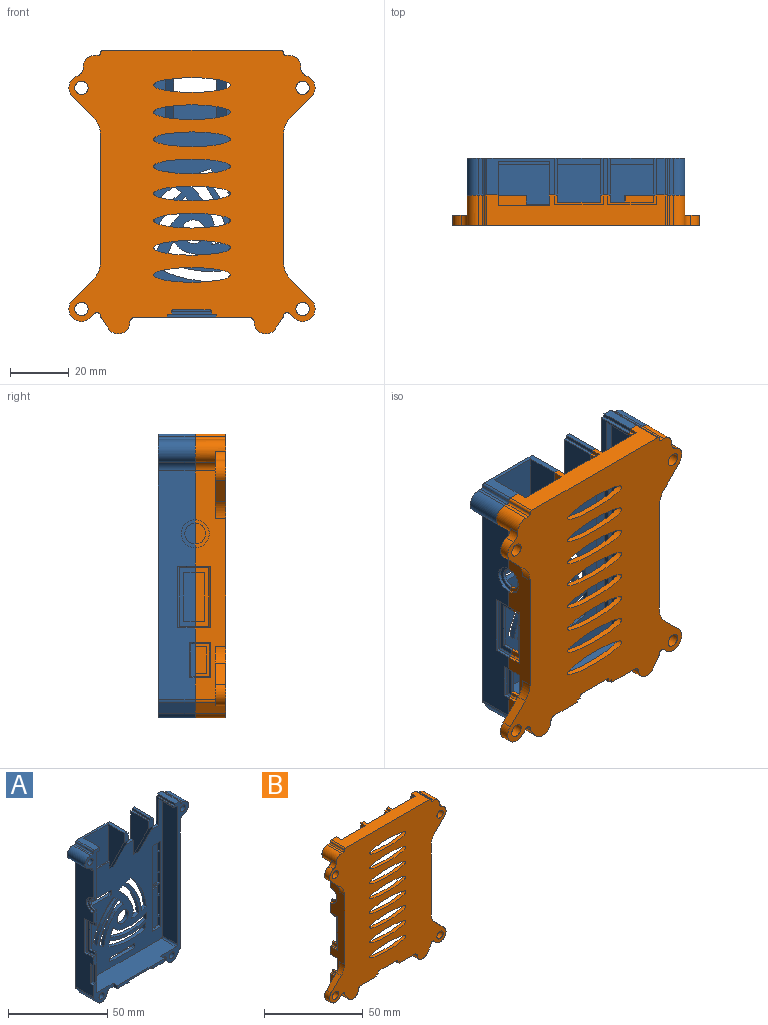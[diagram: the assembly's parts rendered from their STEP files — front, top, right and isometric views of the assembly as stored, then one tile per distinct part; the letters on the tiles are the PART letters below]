
ASSEMBLY  parts=2 mates=1
PART A: 207 faces, bbox 73.8x15.5x96.3 mm
  f0: plane 96.25x73.8mm, normal (0,1,0), area 4343.7mm2, adj f1,f2,f3,f4,f5,f6,f8,f9
  f1: cylinder r=38.11mm len=2.81mm, axis (0,1,0), area 7.6mm2, adj f0,f3,f6,f7
  f2: cylinder r=38.11mm len=3.17mm, axis (0,1,0), area 7.6mm2, adj f0,f7,f27,f28
  f3: cylinder r=34.77mm len=21.39mm, axis (0,-1,0), area 52.8mm2, adj f0,f1,f4,f7
  f4: cylinder r=25.5mm len=2.73mm, axis (0,1,0), area 7mm2, adj f0,f3,f6,f7
  f5: cylinder r=25.5mm len=4.42mm, axis (0,1,0), area 11.1mm2, adj f0,f7,f27,f29
  f6: cylinder r=38.11mm len=21mm, axis (0,1,0), area 52mm2, adj f0,f1,f4,f7
  f7: plane 86.6x58mm, normal (0,-1,0), area 3024.7mm2, adj f1,f2,f3,f4,f5,f6,f8,f9
  f8: cylinder r=38.11mm len=3.71mm, axis (0,1,0), area 7.6mm2, adj f0,f7,f10,f13
  f9: cylinder r=38.11mm len=3.78mm, axis (0,1,0), area 7.6mm2, adj f0,f7,f14,f16
  f10: cylinder r=34.77mm len=25.71mm, axis (0,-1,0), area 52.8mm2, adj f0,f7,f8,f11
  f11: cylinder r=25.5mm len=3.44mm, axis (0,1,0), area 7mm2, adj f0,f7,f10,f13
  f12: cylinder r=25.5mm len=5.08mm, axis (0,1,0), area 11.1mm2, adj f0,f7,f14,f15
  f13: cylinder r=38.11mm len=25.42mm, axis (0,1,0), area 52mm2, adj f0,f7,f8,f11
  f14: cylinder r=32.83mm len=25.5mm, axis (0,-1,0), area 52.5mm2, adj f0,f7,f9,f12
  f15: cylinder r=7.38mm len=4.78mm, axis (0,1,0), area 12.9mm2, adj f0,f7,f12,f16
  f16: cylinder r=29.38mm len=18.77mm, axis (0,1,0), area 38.3mm2, adj f0,f7,f9,f15
  f17: cylinder r=38.11mm len=3.62mm, axis (0,1,0), area 7.6mm2, adj f0,f7,f19,f22
  f18: cylinder r=38.11mm len=3.38mm, axis (0,1,0), area 7.6mm2, adj f0,f7,f23,f25
  f19: cylinder r=34.77mm len=23.14mm, axis (0,-1,0), area 52.8mm2, adj f0,f7,f17,f20
  f20: cylinder r=25.5mm len=3.24mm, axis (0,1,0), area 7mm2, adj f0,f7,f19,f22
  f21: cylinder r=25.5mm len=5.48mm, axis (0,1,0), area 11.1mm2, adj f0,f7,f23,f24
  f22: cylinder r=38.11mm len=23.03mm, axis (0,1,0), area 52mm2, adj f0,f7,f17,f20
  f23: cylinder r=32.83mm len=22.84mm, axis (0,-1,0), area 52.5mm2, adj f0,f7,f18,f21
  f24: cylinder r=7.38mm len=6.15mm, axis (0,1,0), area 12.9mm2, adj f0,f7,f21,f25
  f25: cylinder r=29.38mm len=15.65mm, axis (0,1,0), area 38.3mm2, adj f0,f7,f18,f24
  f26: cylinder r=4mm len=8mm, axis (0,1,0), area 50.3mm2, adj f0,f7
  f27: cylinder r=32.83mm len=21.32mm, axis (0,-1,0), area 52.5mm2, adj f0,f2,f5,f7
  f28: cylinder r=29.38mm len=16.85mm, axis (0,1,0), area 38.3mm2, adj f0,f2,f7,f29
  f29: cylinder r=7.38mm len=5.88mm, axis (0,1,0), area 12.9mm2, adj f0,f5,f7,f28
  f30: plane 16x2mm, normal (0,0,1), area 32mm2, adj f0,f7,f31,f37
  f31: cylinder r=1mm len=2mm, axis (0,-1,0), area 3.1mm2, adj f0,f7,f30,f32
  f32: plane 2x0.8mm, normal (-1,0,0), area 1.6mm2, adj f0,f7,f31,f33
  f33: cylinder r=1mm len=2mm, axis (0,-1,0), area 3.1mm2, adj f0,f7,f32,f34
  f34: plane 16x2mm, normal (0,0,-1), area 32mm2, adj f0,f7,f33,f35
  f35: cylinder r=1mm len=2mm, axis (0,-1,0), area 3.1mm2, adj f0,f7,f34,f36
  f36: plane 2x0.8mm, normal (1,0,0), area 1.6mm2, adj f0,f7,f35,f37
  f37: cylinder r=1mm len=2mm, axis (0,-1,0), area 3.1mm2, adj f0,f7,f30,f36
  f38: plane 2x0.8mm, normal (-1,0,0), area 1.6mm2, adj f0,f7,f39,f45
  f39: cylinder r=1mm len=2mm, axis (0,-1,0), area 3.1mm2, adj f0,f7,f38,f40
  f40: plane 16x2mm, normal (0,0,-1), area 32mm2, adj f0,f7,f39,f41
  f41: cylinder r=1mm len=2mm, axis (0,-1,0), area 3.1mm2, adj f0,f7,f40,f42
  f42: plane 2x0.8mm, normal (1,0,0), area 1.6mm2, adj f0,f7,f41,f43
  f43: cylinder r=1mm len=2mm, axis (0,-1,0), area 3.1mm2, adj f0,f7,f42,f44
  f44: plane 16x2mm, normal (0,0,1), area 32mm2, adj f0,f7,f43,f45
  f45: cylinder r=1mm len=2mm, axis (0,-1,0), area 3.1mm2, adj f0,f7,f38,f44
  f46: cylinder r=1mm len=10.5mm, axis (0,-1,0), area 16.5mm2, adj f7,f47,f50,f55
  f47: plane 10.5x1.55mm, normal (0,0,-1), area 16.3mm2, adj f7,f46,f50,f90
  f48: plane 10.5x1.75mm, normal (0,0,-1), area 18.4mm2, adj f7,f51,f60,f100
  f49: plane 9.75x2.5mm, normal (0,-1,0), area 16.8mm2, adj f55,f104,f110,f111,f112,f113,f114,f115
  f50: plane 30.25x10.45mm, normal (0,-1,0), area 94.5mm2, adj f46,f47,f55,f82,f90,f103,f104,f105
  f51: plane 96.25x20.3mm, normal (0,-1,0), area 270.9mm2, adj f48,f57,f58,f59,f60,f61,f62,f69
  f52: plane 32.75x14.2mm, normal (0,-1,0), area 96.1mm2, adj f55,f56,f57,f62,f68,f104,f115,f116
  f53: plane 6x3.5mm, normal (0,-1,0), area 18.6mm2, adj f80,f83,f85,f93,f94,f95,f96,f98
  f54: plane 6x2.8mm, normal (0,-1,0), area 15.6mm2, adj f82,f84,f86,f87,f88,f102
  f55: plane 84.6x10.5mm, normal (1,0,0), area 682.2mm2, adj f7,f46,f49,f50,f52,f56,f112,f122
  f56: cylinder r=1mm len=10.5mm, axis (0,1,0), area 16.5mm2, adj f7,f52,f55,f57
  f57: plane 56x13.5mm, normal (0,0,1), area 688.2mm2, adj f7,f51,f52,f56,f58,f61,f64,f68
  f58: cylinder r=1mm len=10.5mm, axis (0,1,0), area 16.5mm2, adj f7,f51,f57,f59
  f59: plane 84.6x10.5mm, normal (-1,0,0), area 888.3mm2, adj f7,f51,f58,f60
  f60: cylinder r=1mm len=10.5mm, axis (0,1,0), area 16.5mm2, adj f7,f48,f51,f59
  f61: plane 3x2mm, normal (1,0,0), area 6mm2, adj f51,f57,f62,f64
  f62: plane 38.21x15.5mm, normal (0,0,-1), area 553.1mm2, adj f0,f51,f52,f61,f63,f64,f66,f67
  f63: plane 1.5x1mm, normal (1,0,0), area 1.5mm2, adj f62,f64,f65,f67
  f64: plane 33.4x2mm, normal (0,-1,0), area 50.3mm2, adj f57,f61,f62,f63,f65,f66,f68
  f65: plane 16.5x1.5mm, normal (0,0,-1), area 24.7mm2, adj f63,f64,f66,f67
  f66: plane 1.5x1mm, normal (-1,0,0), area 1.5mm2, adj f62,f64,f65,f67
  f67: plane 16.5x1mm, normal (0,-1,0), area 16.5mm2, adj f62,f63,f65,f66
  f68: plane 3x2mm, normal (-1,0,0), area 6mm2, adj f52,f57,f62,f64
  f69: cylinder r=2mm len=12.5mm, axis (0,1,0), area 38.2mm2, adj f0,f51,f62,f70
  f70: cylinder r=3.9mm len=12.5mm, axis (0,1,0), area 121.2mm2, adj f0,f51,f69,f71
  f71: plane 12.5x3.48mm, normal (0.82,0,-0.58), area 53.1mm2, adj f0,f51,f70,f72
  f72: cylinder r=2mm len=12.5mm, axis (0,1,0), area 15.3mm2, adj f0,f51,f71,f73
  f73: plane 77.46x12.5mm, normal (1,0,0), area 968.2mm2, adj f0,f51,f72,f75
  f74: plane 12.5x0.18mm, normal (1,0,0), area 2.3mm2, adj f0,f51,f78,f79
  f75: cylinder r=3mm len=12.5mm, axis (0,1,0), area 53.5mm2, adj f0,f51,f73,f76
  f76: cylinder r=3.9mm len=12.5mm, axis (0,1,0), area 146.1mm2, adj f0,f51,f75,f77
  f77: plane 12.5x1.2mm, normal (0,0,1), area 15mm2, adj f0,f51,f76,f78
  f78: cylinder r=0.8mm len=12.5mm, axis (0,-1,0), area 15.7mm2, adj f0,f51,f74,f77
  f79: cylinder r=0.8mm len=12.5mm, axis (0,-1,0), area 15.7mm2, adj f0,f51,f74,f81
  f80: plane 12.5x1.5mm, normal (0,0,1), area 18.8mm2, adj f0,f53,f83,f98
  f81: plane 12.5x2.95mm, normal (0,0,1), area 36.9mm2, adj f0,f51,f79,f99
  f82: plane 22.95x12.5mm, normal (0,0,1), area 90.3mm2, adj f0,f50,f54,f88,f90,f91,f102,f103
  f83: plane 12.5x1.2mm, normal (-1,0,0), area 15mm2, adj f0,f53,f80,f85
  f84: plane 12.5x1mm, normal (0,0,1), area 12.5mm2, adj f0,f54,f86,f102
  f85: plane 12.5x1mm, normal (0,0,1), area 12.5mm2, adj f0,f53,f83,f93
  f86: plane 25.8x12.5mm, normal (1,0,0), area 194.7mm2, adj f0,f7,f54,f84,f87,f92
  f87: plane 21x10.5mm, normal (0,-0.89,-0.45), area 65.7mm2, adj f7,f54,f86,f88
  f88: plane 27x11.3mm, normal (-1,0,0), area 191.4mm2, adj f7,f54,f82,f87,f89,f91
  f89: plane 17.4x0.8mm, normal (0,0,1), area 13.9mm2, adj f7,f88,f90,f91
  f90: plane 22.7x11.3mm, normal (1,0,0), area 39.2mm2, adj f7,f47,f50,f82,f89,f91
  f91: plane 22.7x17.4mm, normal (0,-1,0), area 395mm2, adj f82,f88,f89,f90
  f92: plane 14.5x2mm, normal (0,0,1), area 29mm2, adj f0,f7,f86,f93
  f93: plane 25.8x12.5mm, normal (-1,0,0), area 194.7mm2, adj f0,f7,f53,f85,f92,f94
  f94: plane 21x10.5mm, normal (0,-0.89,-0.45), area 82.2mm2, adj f7,f53,f93,f95
  f95: plane 25.8x12.5mm, normal (1,0,0), area 194.7mm2, adj f0,f7,f53,f94,f96,f101
  f96: plane 12.5x1mm, normal (0,0,1), area 12.5mm2, adj f0,f53,f95,f98
  f97: plane 12.5x1mm, normal (0,0,1), area 12.5mm2, adj f0,f51,f99,f100
  f98: plane 12.5x1.2mm, normal (1,0,0), area 15mm2, adj f0,f53,f80,f96
  f99: plane 12.5x1.2mm, normal (-1,0,0), area 15mm2, adj f0,f51,f81,f97
  f100: plane 17.05x12.5mm, normal (-1,0,0), area 42.5mm2, adj f0,f7,f48,f51,f97,f101
  f101: plane 14.5x2mm, normal (0,0,1), area 29mm2, adj f0,f7,f95,f100
  f102: plane 12.5x1.2mm, normal (1,0,0), area 15mm2, adj f0,f54,f82,f84
  f103: cylinder r=0.8mm len=12.5mm, axis (0,1,0), area 15.7mm2, adj f0,f50,f82,f105
  f104: plane 77.46x12.5mm, normal (-1,0,0), area 784.3mm2, adj f0,f49,f50,f52,f106,f110,f113,f117
  f105: plane 12.5x0.18mm, normal (-1,0,0), area 2.2mm2, adj f0,f50,f103,f109
  f106: cylinder r=3mm len=12.5mm, axis (0,-1,0), area 53.5mm2, adj f0,f50,f104,f107
  f107: cylinder r=3.9mm len=12.5mm, axis (0,1,0), area 146.1mm2, adj f0,f50,f106,f108
  f108: plane 12.5x1.2mm, normal (0,0,1), area 15mm2, adj f0,f50,f107,f109
  f109: cylinder r=0.8mm len=12.5mm, axis (0,1,0), area 15.7mm2, adj f0,f50,f105,f108
  f110: cylinder r=4.75mm len=9.5mm, axis (-1,0,0), area 14.9mm2, adj f49,f50,f104,f111
  f111: plane 9.5x4.75mm, normal (-1,0,0), area 16.2mm2, adj f49,f50,f110,f112
  f112: cylinder r=3.5mm len=7mm, axis (-1,0,0), area 11mm2, adj f49,f50,f55,f111
  f113: plane 5.93x1mm, normal (0,0,-1), area 5.9mm2, adj f49,f104,f114,f118
  f114: plane 5.93x0.5mm, normal (-0.71,0,-0.71), area 4mm2, adj f49,f113,f115,f119
  f115: plane 20x5.43mm, normal (-1,0,0), area 43.8mm2, adj f49,f52,f114,f116,f119,f120,f125,f126
  f116: plane 5.93x0.5mm, normal (-0.71,0,0.71), area 4mm2, adj f52,f115,f117,f119
  f117: plane 5.93x1mm, normal (0,0,1), area 5.9mm2, adj f52,f104,f116,f118
  f118: plane 21x1mm, normal (0,-1,0), area 21mm2, adj f104,f113,f117,f119
  f119: plane 21x0.5mm, normal (-0.71,-0.71,0), area 14.5mm2, adj f114,f115,f116,f118
  f120: plane 3.93x1mm, normal (0,0,-1), area 3.9mm2, adj f49,f115,f121,f126
  f121: plane 23x5.93mm, normal (1,0,0), area 71.5mm2, adj f49,f52,f120,f122,f123,f124,f125,f126
  f122: plane 6.43x0.5mm, normal (0.71,0,0.71), area 4.4mm2, adj f49,f55,f121,f123
  f123: plane 24x0.5mm, normal (0.71,0.71,0), area 16.6mm2, adj f55,f121,f122,f124
  f124: plane 6.43x0.5mm, normal (0.71,0,-0.71), area 4.4mm2, adj f52,f55,f121,f123
  f125: plane 3.93x1mm, normal (0,0,1), area 3.9mm2, adj f52,f115,f121,f126
  f126: plane 16.5x1mm, normal (0,-1,0), area 16.5mm2, adj f115,f120,f121,f125
  f127: plane 2x1mm, normal (0,0,-1), area 2mm2, adj f52,f104,f128,f132
  f128: plane 2x0.5mm, normal (-0.71,0,-0.71), area 1.2mm2, adj f52,f127,f129,f133
  f129: plane 11x1.5mm, normal (-1,0,0), area 16.5mm2, adj f52,f128,f130,f133
  f130: plane 2x0.5mm, normal (-0.71,0,0.71), area 1.2mm2, adj f52,f129,f131,f133
  f131: plane 2x1mm, normal (0,0,1), area 2mm2, adj f52,f104,f130,f132
  f132: plane 12x1mm, normal (0,-1,0), area 12mm2, adj f104,f127,f131,f133
  f133: plane 12x0.5mm, normal (-0.71,-0.71,0), area 8.1mm2, adj f128,f129,f130,f132
  f134: cylinder r=2mm len=12.5mm, axis (0,-1,0), area 15.3mm2, adj f0,f52,f104,f135
  f135: plane 12.5x3.48mm, normal (-0.82,0,-0.58), area 53.1mm2, adj f0,f52,f134,f136
  f136: cylinder r=3.9mm len=12.5mm, axis (0,1,0), area 121.2mm2, adj f0,f52,f135,f137
  f137: cylinder r=2mm len=12.5mm, axis (0,-1,0), area 38.2mm2, adj f0,f52,f62,f136
  f138: plane 2.5x0.5mm, normal (0.71,0,-0.71), area 1.6mm2, adj f52,f55,f139,f141
  f139: plane 12x2mm, normal (1,0,0), area 24mm2, adj f52,f138,f140,f141
  f140: plane 2.5x0.5mm, normal (0.71,0,0.71), area 1.6mm2, adj f52,f55,f139,f141
  f141: plane 13x0.5mm, normal (0.71,0.71,0), area 8.8mm2, adj f55,f138,f139,f140
  f142: cylinder r=1.9mm len=11.5mm, axis (0,1,0), area 137.3mm2, adj f51,f145
  f143: plane 5.8x5.8mm, normal (0,1,0), area 15.1mm2, adj f147,f153
  f144: plane 5.8x5.8mm, normal (0,1,0), area 15.1mm2, adj f148,f152
  f145: plane 5.8x5.8mm, normal (0,1,0), area 15.1mm2, adj f142,f149
  f146: plane 5.8x5.8mm, normal (0,1,0), area 15.1mm2, adj f150,f151
  f147: cylinder r=2.9mm len=5.8mm, axis (0,1,0), area 18.2mm2, adj f0,f143
  f148: cylinder r=2.9mm len=5.8mm, axis (0,1,0), area 18.2mm2, adj f0,f144
  f149: cylinder r=2.9mm len=5.8mm, axis (0,1,0), area 18.2mm2, adj f0,f145
  f150: cylinder r=2.9mm len=5.8mm, axis (0,1,0), area 18.2mm2, adj f0,f146
  f151: cylinder r=1.9mm len=11.5mm, axis (0,1,0), area 137.3mm2, adj f50,f146
  f152: cylinder r=1.9mm len=11.5mm, axis (0,-1,0), area 137.3mm2, adj f51,f144
  f153: cylinder r=1.9mm len=11.5mm, axis (0,-1,0), area 137.3mm2, adj f52,f143
  f154: plane 6x2mm, normal (0,0,-1), area 11mm2, adj f0,f7,f155,f161,f174,f186,f198
  f155: plane 52.7x6mm, normal (0,-1,0), area 208.8mm2, adj f154,f156,f157,f158,f159,f160,f161,f162
  f156: plane 2.5x1mm, normal (0,0,-1), area 2.5mm2, adj f0,f155,f157,f161
  f157: plane 1x1mm, normal (-1,0,0), area 1mm2, adj f0,f155,f156,f158
  f158: plane 1.5x1mm, normal (0,0,1), area 1.5mm2, adj f0,f155,f157,f159
  f159: plane 4.96x1mm, normal (-1,0,0), area 5mm2, adj f0,f155,f158,f160
  f160: plane 1x1mm, normal (0,0,1), area 1mm2, adj f0,f155,f159,f161
  f161: plane 52.7x2mm, normal (1,0,0), area 100.4mm2, adj f0,f7,f154,f155,f156,f160,f162,f164
  f162: plane 1x1mm, normal (0,0,-1), area 1mm2, adj f0,f155,f161,f163
  f163: plane 11.93x1mm, normal (-1,0,0), area 11.9mm2, adj f0,f155,f162,f164
  f164: plane 1x1mm, normal (0,0,1), area 1mm2, adj f0,f155,f161,f163
  f165: plane 1x1mm, normal (0,0,-1), area 1mm2, adj f0,f155,f161,f166
  f166: plane 4.96x1mm, normal (-1,0,0), area 5mm2, adj f0,f155,f165,f167
  f167: plane 1.5x1mm, normal (0,0,-1), area 1.5mm2, adj f0,f155,f166,f168
  f168: plane 1x1mm, normal (-1,0,0), area 1mm2, adj f0,f155,f167,f169
  f169: plane 6x2mm, normal (0,0,1), area 11mm2, adj f0,f7,f155,f161,f168,f170,f174
  f170: plane 1x1mm, normal (1,0,0), area 1mm2, adj f0,f155,f169,f171
  f171: plane 1.5x1mm, normal (0,0,-1), area 1.5mm2, adj f0,f155,f170,f172
  f172: plane 4.96x1mm, normal (1,0,0), area 5mm2, adj f0,f155,f171,f173
  f173: plane 1x1mm, normal (0,0,-1), area 1mm2, adj f0,f155,f172,f174
  f174: plane 52.7x2mm, normal (-1,0,0), area 100.4mm2, adj f0,f7,f154,f155,f169,f173,f175,f179
  f175: plane 2.5x1mm, normal (0,0,1), area 2.5mm2, adj f0,f155,f174,f176
  f176: plane 1x1mm, normal (1,0,0), area 1mm2, adj f0,f155,f175,f177
  f177: plane 1.5x1mm, normal (0,0,-1), area 1.5mm2, adj f0,f155,f176,f178
  f178: plane 4.96x1mm, normal (1,0,0), area 5mm2, adj f0,f155,f177,f179
  f179: plane 1x1mm, normal (0,0,-1), area 1mm2, adj f0,f155,f174,f178
  f180: plane 1x1mm, normal (0,0,1), area 1mm2, adj f0,f155,f174,f181
  f181: plane 11.93x1mm, normal (1,0,0), area 11.9mm2, adj f0,f155,f180,f182
  f182: plane 1x1mm, normal (0,0,-1), area 1mm2, adj f0,f155,f174,f181
  f183: plane 1x1mm, normal (0,0,1), area 1mm2, adj f0,f155,f174,f184
  f184: plane 4.96x1mm, normal (1,0,0), area 5mm2, adj f0,f155,f183,f185
  f185: plane 1.5x1mm, normal (0,0,1), area 1.5mm2, adj f0,f155,f184,f186
  f186: plane 1x1mm, normal (1,0,0), area 1mm2, adj f0,f154,f155,f185
  f187: plane 1x1mm, normal (0,0,1), area 1mm2, adj f0,f155,f174,f188
  f188: plane 11.93x1mm, normal (1,0,0), area 11.9mm2, adj f0,f155,f187,f189
  f189: plane 1x1mm, normal (0,0,-1), area 1mm2, adj f0,f155,f174,f188
  f190: plane 1x1mm, normal (0,0,1), area 1mm2, adj f0,f155,f174,f191
  f191: plane 4.96x1mm, normal (1,0,0), area 5mm2, adj f0,f155,f190,f192
  f192: plane 1.5x1mm, normal (0,0,1), area 1.5mm2, adj f0,f155,f191,f193
  f193: plane 1x1mm, normal (1,0,0), area 1mm2, adj f0,f155,f192,f194
  f194: plane 2.5x1mm, normal (0,0,-1), area 2.5mm2, adj f0,f155,f174,f193
  f195: plane 1x1mm, normal (0,0,1), area 1mm2, adj f0,f155,f161,f196
  f196: plane 4.96x1mm, normal (-1,0,0), area 5mm2, adj f0,f155,f195,f197
  f197: plane 1.5x1mm, normal (0,0,1), area 1.5mm2, adj f0,f155,f196,f198
  f198: plane 1x1mm, normal (-1,0,0), area 1mm2, adj f0,f154,f155,f197
  f199: plane 1x1mm, normal (0,0,-1), area 1mm2, adj f0,f155,f161,f200
  f200: plane 11.93x1mm, normal (-1,0,0), area 11.9mm2, adj f0,f155,f199,f201
  f201: plane 1x1mm, normal (0,0,1), area 1mm2, adj f0,f155,f161,f200
  f202: plane 1x1mm, normal (0,0,-1), area 1mm2, adj f0,f155,f161,f203
  f203: plane 4.96x1mm, normal (-1,0,0), area 5mm2, adj f0,f155,f202,f204
  f204: plane 1.5x1mm, normal (0,0,-1), area 1.5mm2, adj f0,f155,f203,f205
  f205: plane 1x1mm, normal (-1,0,0), area 1mm2, adj f0,f155,f204,f206
  f206: plane 2.5x1mm, normal (0,0,1), area 2.5mm2, adj f0,f155,f161,f205
PART B: 170 faces, bbox 83.8x10.6x96.6 mm
  f0: plane 96.58x83.83mm, normal (0,-1,0), area 5317.9mm2, adj f1,f6,f7,f8,f9,f37,f38,f39
  f1: cylinder r=2.25mm len=4.5mm, axis (0,-1,0), area 49.5mm2, adj f0,f3
  f2: plane 22.79x10.75mm, normal (0,1,0), area 100.2mm2, adj f8,f9,f93,f123,f124,f125,f126,f127
  f3: plane 22.79x10.75mm, normal (0,1,0), area 100.2mm2, adj f1,f39,f152,f153,f154,f155,f156,f157
  f4: plane 20.07x10.76mm, normal (0,1,0), area 93.7mm2, adj f6,f39,f41,f147,f148,f149,f150,f151
  f5: plane 20.07x10.76mm, normal (0,1,0), area 93.7mm2, adj f7,f93,f128,f129,f130,f131,f132,f133
  f6: cylinder r=2.25mm len=4.5mm, axis (0,-1,0), area 49.5mm2, adj f0,f4
  f7: cylinder r=2.25mm len=4.5mm, axis (0,-1,0), area 49.5mm2, adj f0,f5
  f8: cylinder r=2.25mm len=4.5mm, axis (0,-1,0), area 49.5mm2, adj f0,f2
  f9: cylinder r=3.9mm len=10.3mm, axis (0,-1,0), area 101.4mm2, adj f0,f2,f12,f123,f127,f139
  f10: plane 3x2.8mm, normal (0,1,0), area 7.2mm2, adj f25,f28,f30,f37,f162,f163
  f11: plane 3.5x3mm, normal (0,1,0), area 8.1mm2, adj f29,f32,f35,f37,f163,f164,f167,f169
  f12: plane 30.25x10.45mm, normal (0,1,0), area 99.5mm2, adj f9,f22,f26,f37,f89,f90,f91,f92
  f13: plane 8.65x2.5mm, normal (0,1,0), area 15.1mm2, adj f89,f93,f95,f96,f97,f98,f100,f101
  f14: plane 9.75x2.5mm, normal (0,1,0), area 16.8mm2, adj f89,f90,f91,f92,f93,f98,f101,f107
  f15: plane 15.1x14.15mm, normal (0,1,0), area 78mm2, adj f17,f46,f82,f88,f89,f93,f97,f99
  f16: plane 96.25x20.25mm, normal (0,1,0), area 280.9mm2, adj f23,f24,f26,f34,f35,f36,f37,f38
  f17: cylinder r=1.4mm len=8.3mm, axis (0,-1,0), area 73mm2, adj f15,f20
  f18: plane 2.8x2.8mm, normal (0,1,0), area 6.2mm2, adj f22
  f19: plane 2.8x2.8mm, normal (0,1,0), area 6.2mm2, adj f23
  f20: plane 2.8x2.8mm, normal (0,1,0), area 6.2mm2, adj f17
  f21: plane 2.8x2.8mm, normal (0,1,0), area 6.2mm2, adj f24
  f22: cylinder r=1.4mm len=8.3mm, axis (0,-1,0), area 73mm2, adj f12,f18
  f23: cylinder r=1.4mm len=8.3mm, axis (0,1,0), area 73mm2, adj f16,f19
  f24: cylinder r=1.4mm len=8.3mm, axis (0,-1,0), area 73mm2, adj f16,f21
  f25: plane 3.6x3mm, normal (-1,0,0), area 8.7mm2, adj f10,f26,f27,f30,f37,f161
  f26: plane 57x8.3mm, normal (0,0,-1), area 322.8mm2, adj f12,f16,f25,f27,f28,f31,f32,f33
  f27: plane 2.8x2mm, normal (0,-0.45,-0.89), area 6.3mm2, adj f25,f26,f28,f30
  f28: plane 2.55x1.8mm, normal (1,0,0), area 3.5mm2, adj f10,f26,f27,f30,f163,f168
  f29: plane 3.5x0.55mm, normal (0,0,-1), area 1.9mm2, adj f11,f31,f32,f169
  f30: plane 2.8x0.55mm, normal (0,0,-1), area 1.5mm2, adj f10,f25,f27,f28
  f31: plane 3.5x2mm, normal (0,-0.45,-0.89), area 7.8mm2, adj f26,f29,f32,f169
  f32: plane 2.55x1.8mm, normal (1,0,0), area 3.5mm2, adj f11,f26,f29,f31,f33,f35
  f33: plane 14.5x0.8mm, normal (0,1,0), area 11.6mm2, adj f26,f32,f34,f35
  f34: plane 2.47x0.8mm, normal (-1,0,0), area 2mm2, adj f16,f26,f33,f35
  f35: plane 16.5x3.17mm, normal (0,0,1), area 16.5mm2, adj f11,f16,f32,f33,f34,f36,f166,f167
  f36: plane 3.17x1.2mm, normal (-1,0,0), area 3.8mm2, adj f16,f35,f37,f166
  f37: plane 60.4x10.3mm, normal (0,0,1), area 454.9mm2, adj f0,f10,f11,f12,f16,f25,f36,f38
  f38: cylinder r=0.8mm len=10.3mm, axis (0,-1,0), area 12.9mm2, adj f0,f16,f37,f40
  f39: plane 77.46x10.3mm, normal (1,0,0), area 678.5mm2, adj f0,f3,f4,f16,f41,f151,f152,f157
  f40: plane 10.3x0.18mm, normal (1,0,0), area 1.9mm2, adj f0,f16,f38,f159
  f41: cylinder r=2mm len=10.3mm, axis (0,1,0), area 12.1mm2, adj f0,f4,f16,f39,f42,f147
  f42: plane 10.3x3.48mm, normal (0.82,0,-0.58), area 43.8mm2, adj f0,f16,f41,f43
  f43: cylinder r=3.9mm len=10.3mm, axis (0,-1,0), area 99.9mm2, adj f0,f16,f42,f44
  f44: cylinder r=2mm len=10.3mm, axis (0,1,0), area 31.5mm2, adj f0,f16,f43,f45
  f45: plane 10.96x10.3mm, normal (0,0,-1), area 87.3mm2, adj f0,f16,f44,f47,f83,f84
  f46: plane 10.76x10.3mm, normal (0,0,-1), area 85.3mm2, adj f0,f15,f136,f141,f142,f146
  f47: plane 7.3x1mm, normal (-1,0,0), area 7.3mm2, adj f0,f45,f48,f83
  f48: plane 7.3x1.5mm, normal (0,0,-1), area 10.9mm2, adj f0,f47,f50,f83
  f49: plane 7.3x1.5mm, normal (0,0,-1), area 11mm2, adj f0,f142,f143,f146
  f50: plane 7.3x1mm, normal (-1,0,0), area 7.3mm2, adj f0,f48,f51,f81,f83
  f51: cylinder r=0.5mm len=2mm, axis (0,-1,0), area 1.6mm2, adj f0,f50,f52,f145
  f52: plane 86.93x58.33mm, normal (0,1,0), area 4054.4mm2, adj f26,f51,f53,f54,f55,f56,f57,f58
  f53: extruded ~26x5mm, area 109.1mm2, adj f0,f52
  f54: extruded ~26x5mm, area 109.1mm2, adj f0,f52
  f55: extruded ~26x5mm, area 109.1mm2, adj f0,f52
  f56: extruded ~26x5mm, area 109.1mm2, adj f0,f52
  f57: extruded ~26x5mm, area 109.1mm2, adj f0,f52
  f58: extruded ~26x5mm, area 109.1mm2, adj f0,f52
  f59: extruded ~26x5mm, area 109.1mm2, adj f0,f52
  f60: extruded ~26x5mm, area 109.1mm2, adj f0,f52
  f61: cone r=3.15mm half-angle=45deg, axis (0,-1,0), area 14mm2, adj f52,f62
  f62: cylinder r=2.9mm len=5.8mm, axis (0,1,0), area 63.8mm2, adj f61,f64
  f63: plane 5.8x5.8mm, normal (0,1,0), area 20.3mm2, adj f67,f69
  f64: plane 5.8x5.8mm, normal (0,1,0), area 20.3mm2, adj f62,f74
  f65: plane 5.8x5.8mm, normal (0,1,0), area 20.3mm2, adj f76,f77
  f66: plane 5.8x5.8mm, normal (0,1,0), area 20.3mm2, adj f75,f79
  f67: cylinder r=2.9mm len=5.8mm, axis (0,1,0), area 63.8mm2, adj f63,f68
  f68: cone r=3.15mm half-angle=45deg, axis (0,-1,0), area 14mm2, adj f52,f67
  f69: cylinder r=1.4mm len=5mm, axis (0,1,0), area 44mm2, adj f63,f72
  f70: plane 2.8x2.8mm, normal (0,1,0), area 6.2mm2, adj f74
  f71: plane 2.8x2.8mm, normal (0,1,0), area 6.2mm2, adj f75
  f72: plane 2.8x2.8mm, normal (0,1,0), area 6.2mm2, adj f69
  f73: plane 2.8x2.8mm, normal (0,1,0), area 6.2mm2, adj f76
  f74: cylinder r=1.4mm len=5mm, axis (0,1,0), area 44mm2, adj f64,f70
  f75: cylinder r=1.4mm len=5mm, axis (0,1,0), area 44mm2, adj f66,f71
  f76: cylinder r=1.4mm len=5mm, axis (0,1,0), area 44mm2, adj f65,f73
  f77: cylinder r=2.9mm len=5.8mm, axis (0,1,0), area 63.8mm2, adj f65,f78
  f78: cone r=3.15mm half-angle=45deg, axis (0,-1,0), area 14mm2, adj f52,f77
  f79: cylinder r=2.9mm len=5.8mm, axis (0,1,0), area 63.8mm2, adj f66,f80
  f80: cone r=3.15mm half-angle=45deg, axis (0,-1,0), area 14mm2, adj f52,f79
  f81: plane 21.85x8.3mm, normal (0,0,1), area 151.4mm2, adj f16,f50,f52,f83,f84,f85
  f82: plane 21.65x8.3mm, normal (0,0,1), area 149.7mm2, adj f15,f52,f88,f141,f142,f143
  f83: plane 10x2mm, normal (0,1,0), area 18.5mm2, adj f45,f47,f48,f50,f81,f84
  f84: plane 3x2mm, normal (-1,0,0), area 6mm2, adj f16,f45,f81,f83
  f85: cylinder r=0.5mm len=8.3mm, axis (0,1,0), area 6.5mm2, adj f16,f52,f81,f86
  f86: plane 85.6x8.3mm, normal (-1,0,0), area 710.5mm2, adj f16,f52,f85,f87
  f87: cylinder r=0.5mm len=8.3mm, axis (0,1,0), area 6.5mm2, adj f16,f26,f52,f86
  f88: cylinder r=0.5mm len=8.3mm, axis (0,1,0), area 6.5mm2, adj f15,f52,f82,f89
  f89: plane 85.6x8.3mm, normal (1,0,0), area 494.1mm2, adj f12,f13,f14,f15,f52,f88,f90,f102
  f90: cylinder r=3.5mm len=7mm, axis (-1,0,0), area 11mm2, adj f12,f14,f89,f91
  f91: plane 9.5x4.75mm, normal (-1,0,0), area 16.2mm2, adj f12,f14,f90,f92
  f92: cylinder r=4.75mm len=9.5mm, axis (-1,0,0), area 14.9mm2, adj f12,f14,f91,f93
  f93: plane 77.46x10.3mm, normal (-1,0,0), area 472.5mm2, adj f0,f2,f5,f12,f13,f14,f15,f92
  f94: plane 10.3x0.18mm, normal (-1,0,0), area 1.9mm2, adj f0,f12,f137,f138
  f95: plane 5.12x1mm, normal (0,0,1), area 5.1mm2, adj f13,f93,f96,f121
  f96: plane 5.12x0.5mm, normal (-0.71,0,0.71), area 3.4mm2, adj f13,f95,f98,f122
  f97: plane 11x4.75mm, normal (-1,0,0), area 18.5mm2, adj f13,f15,f99,f105,f106,f113,f116,f117
  f98: plane 20x4.62mm, normal (-1,0,0), area 40.9mm2, adj f13,f14,f96,f107,f108,f109,f119,f122
  f99: plane 3.75x1mm, normal (0,0,1), area 3.8mm2, adj f15,f97,f100,f106
  f100: plane 14x5.25mm, normal (1,0,0), area 39.8mm2, adj f13,f15,f99,f102,f103,f104,f105,f106
  f101: plane 23x3.62mm, normal (1,0,0), area 31.8mm2, adj f13,f14,f107,f108,f109,f110,f111,f112
  f102: plane 5.75x0.5mm, normal (0.71,0,-0.71), area 3.9mm2, adj f15,f89,f100,f103
  f103: plane 15x0.5mm, normal (0.71,-0.71,0), area 10.3mm2, adj f89,f100,f102,f104
  f104: plane 5.75x0.5mm, normal (0.71,0,0.71), area 3.9mm2, adj f13,f89,f100,f103
  f105: plane 3.75x1mm, normal (0,0,-1), area 3.8mm2, adj f13,f97,f100,f106
  f106: plane 9x1mm, normal (0,1,0), area 9mm2, adj f97,f99,f100,f105
  f107: plane 3.12x1mm, normal (0,0,-1), area 3.1mm2, adj f14,f98,f101,f108
  f108: plane 16.5x1mm, normal (0,1,0), area 16.5mm2, adj f98,f101,f107,f109
  f109: plane 3.12x1mm, normal (0,0,1), area 3.1mm2, adj f13,f98,f101,f108
  f110: plane 4.62x0.5mm, normal (0.71,0,-0.71), area 2.9mm2, adj f13,f89,f101,f111
  f111: plane 24x1mm, normal (0.89,-0.45,0), area 26.3mm2, adj f89,f101,f110,f112
  f112: plane 4.62x0.5mm, normal (0.71,0,0.71), area 2.9mm2, adj f14,f89,f101,f111
  f113: plane 5.25x0.5mm, normal (-0.71,0,-0.71), area 3.5mm2, adj f13,f97,f114,f116
  f114: plane 5.25x1mm, normal (0,0,-1), area 5.2mm2, adj f13,f93,f113,f115
  f115: plane 12x1mm, normal (0,1,0), area 12mm2, adj f93,f114,f116,f118
  f116: plane 12x0.5mm, normal (-0.71,0.71,0), area 8.1mm2, adj f97,f113,f115,f117
  f117: plane 5.25x0.5mm, normal (-0.71,0,0.71), area 3.5mm2, adj f15,f97,f116,f118
  f118: plane 5.25x1mm, normal (0,0,1), area 5.2mm2, adj f15,f93,f115,f117
  f119: plane 5.12x0.5mm, normal (-0.71,0,-0.71), area 3.4mm2, adj f14,f98,f120,f122
  f120: plane 5.12x1mm, normal (0,0,-1), area 5.1mm2, adj f14,f93,f119,f121
  f121: plane 21x1mm, normal (0,1,0), area 21mm2, adj f93,f95,f120,f122
  f122: plane 21x0.5mm, normal (-0.71,0.71,0), area 14.5mm2, adj f96,f98,f119,f121
  f123: cylinder r=3mm len=6.8mm, axis (0,-1,0), area 29.1mm2, adj f2,f9,f12,f93
  f124: cylinder r=8mm len=5.66mm, axis (0,-1,0), area 22mm2, adj f0,f2,f93,f125
  f125: plane 7.16x7.16mm, normal (-0.71,0,-0.71), area 35.5mm2, adj f0,f2,f124,f126
  f126: cylinder r=4.25mm len=7.02mm, axis (0,-1,0), area 30mm2, adj f0,f2,f125,f127
  f127: cylinder r=3mm len=3.5mm, axis (0,-1,0), area 13.4mm2, adj f0,f2,f9,f126
  f128: cylinder r=8mm len=5.66mm, axis (0,1,0), area 22mm2, adj f0,f5,f93,f129
  f129: plane 7.16x7.16mm, normal (-0.71,0,0.71), area 35.5mm2, adj f0,f5,f128,f130
  f130: cylinder r=4.25mm len=7.26mm, axis (0,-1,0), area 46.7mm2, adj f0,f5,f129,f131
  f131: plane 3.5x1.45mm, normal (0.71,0,-0.71), area 7.2mm2, adj f0,f5,f130,f132
  f132: cylinder r=1.2mm len=3.5mm, axis (0,-1,0), area 9.6mm2, adj f0,f5,f131,f133
  f133: cylinder r=2mm len=10.3mm, axis (0,-1,0), area 12.1mm2, adj f0,f5,f15,f93,f132,f134
  f134: plane 10.3x3.48mm, normal (-0.82,0,-0.58), area 43.8mm2, adj f0,f15,f133,f135
  f135: cylinder r=3.9mm len=10.3mm, axis (0,-1,0), area 99.9mm2, adj f0,f15,f134,f136
  f136: cylinder r=2mm len=10.3mm, axis (0,-1,0), area 31.5mm2, adj f0,f15,f46,f135
  f137: cylinder r=0.8mm len=10.3mm, axis (0,1,0), area 12.9mm2, adj f0,f12,f37,f94
  f138: cylinder r=0.8mm len=10.3mm, axis (0,1,0), area 12.9mm2, adj f0,f12,f94,f139
  f139: plane 10.3x1.2mm, normal (0,0,1), area 12.4mm2, adj f0,f9,f12,f138
  f140: cylinder r=0.5mm len=8.3mm, axis (0,-1,0), area 6.5mm2, adj f12,f26,f52,f89
  f141: plane 3x2mm, normal (1,0,0), area 6mm2, adj f15,f46,f82,f142
  f142: plane 10x2mm, normal (0,1,0), area 18.5mm2, adj f46,f49,f82,f141,f143,f146
  f143: plane 7.3x1mm, normal (1,0,0), area 7.3mm2, adj f0,f49,f82,f142,f144
  f144: cylinder r=0.5mm len=2mm, axis (0,-1,0), area 1.6mm2, adj f0,f52,f143,f145
  f145: plane 12.5x2mm, normal (0,0,-1), area 25mm2, adj f0,f51,f52,f144
  f146: plane 7.3x1mm, normal (1,0,0), area 7.3mm2, adj f0,f46,f49,f142
  f147: cylinder r=1.2mm len=3.5mm, axis (0,1,0), area 9.6mm2, adj f0,f4,f41,f148
  f148: plane 3.5x1.45mm, normal (-0.71,0,-0.71), area 7.2mm2, adj f0,f4,f147,f149
  f149: cylinder r=4.25mm len=7.26mm, axis (0,-1,0), area 46.7mm2, adj f0,f4,f148,f150
  f150: plane 7.16x7.16mm, normal (0.71,0,0.71), area 35.5mm2, adj f0,f4,f149,f151
  f151: cylinder r=8mm len=5.66mm, axis (0,-1,0), area 22mm2, adj f0,f4,f39,f150
  f152: cylinder r=8mm len=5.66mm, axis (0,1,0), area 22mm2, adj f0,f3,f39,f153
  f153: plane 7.16x7.16mm, normal (0.71,0,-0.71), area 35.5mm2, adj f0,f3,f152,f154
  f154: cylinder r=4.25mm len=7.02mm, axis (0,-1,0), area 30mm2, adj f0,f3,f153,f155
  f155: cylinder r=3mm len=3.5mm, axis (0,1,0), area 13.4mm2, adj f0,f3,f154,f156
  f156: cylinder r=3.9mm len=10.3mm, axis (0,1,0), area 101.4mm2, adj f0,f3,f16,f155,f157,f158
  f157: cylinder r=3mm len=6.8mm, axis (0,1,0), area 29.1mm2, adj f3,f16,f39,f156
  f158: plane 10.3x1.2mm, normal (0,0,1), area 12.4mm2, adj f0,f16,f156,f159
  f159: cylinder r=0.8mm len=10.3mm, axis (0,-1,0), area 12.9mm2, adj f0,f16,f40,f158
  f160: plane 3.6x2mm, normal (1,0,0), area 7.2mm2, adj f12,f26,f37,f161
  f161: plane 17.4x2mm, normal (0,1,0), area 34.8mm2, adj f25,f26,f37,f160
  f162: plane 3.17x1.2mm, normal (1,0,0), area 3.8mm2, adj f10,f37,f163,f165
  f163: plane 16.5x3.17mm, normal (0,0,1), area 16.5mm2, adj f10,f11,f28,f162,f164,f165,f168,f169
  f164: plane 3.17x1.2mm, normal (-1,0,0), area 3.8mm2, adj f11,f37,f163,f165
  f165: plane 16.5x1.2mm, normal (0,1,0), area 19.8mm2, adj f37,f162,f163,f164
  f166: plane 16.5x1.2mm, normal (0,1,0), area 19.8mm2, adj f35,f36,f37,f167
  f167: plane 3.17x1.2mm, normal (1,0,0), area 3.8mm2, adj f11,f35,f37,f166
  f168: plane 14.5x0.8mm, normal (0,1,0), area 11.6mm2, adj f26,f28,f163,f169
  f169: plane 2.55x1.8mm, normal (-1,0,0), area 3.5mm2, adj f11,f26,f29,f31,f163,f168
PLACE A t=(-11.72,-58.1,13.47)mm
PLACE B t=(-11.72,-78.9,13.47)mm
MATE cylindrical A.f76 <-> B.f23  axis (0,1,0) through (52.28,-68.6,3.39)mm
